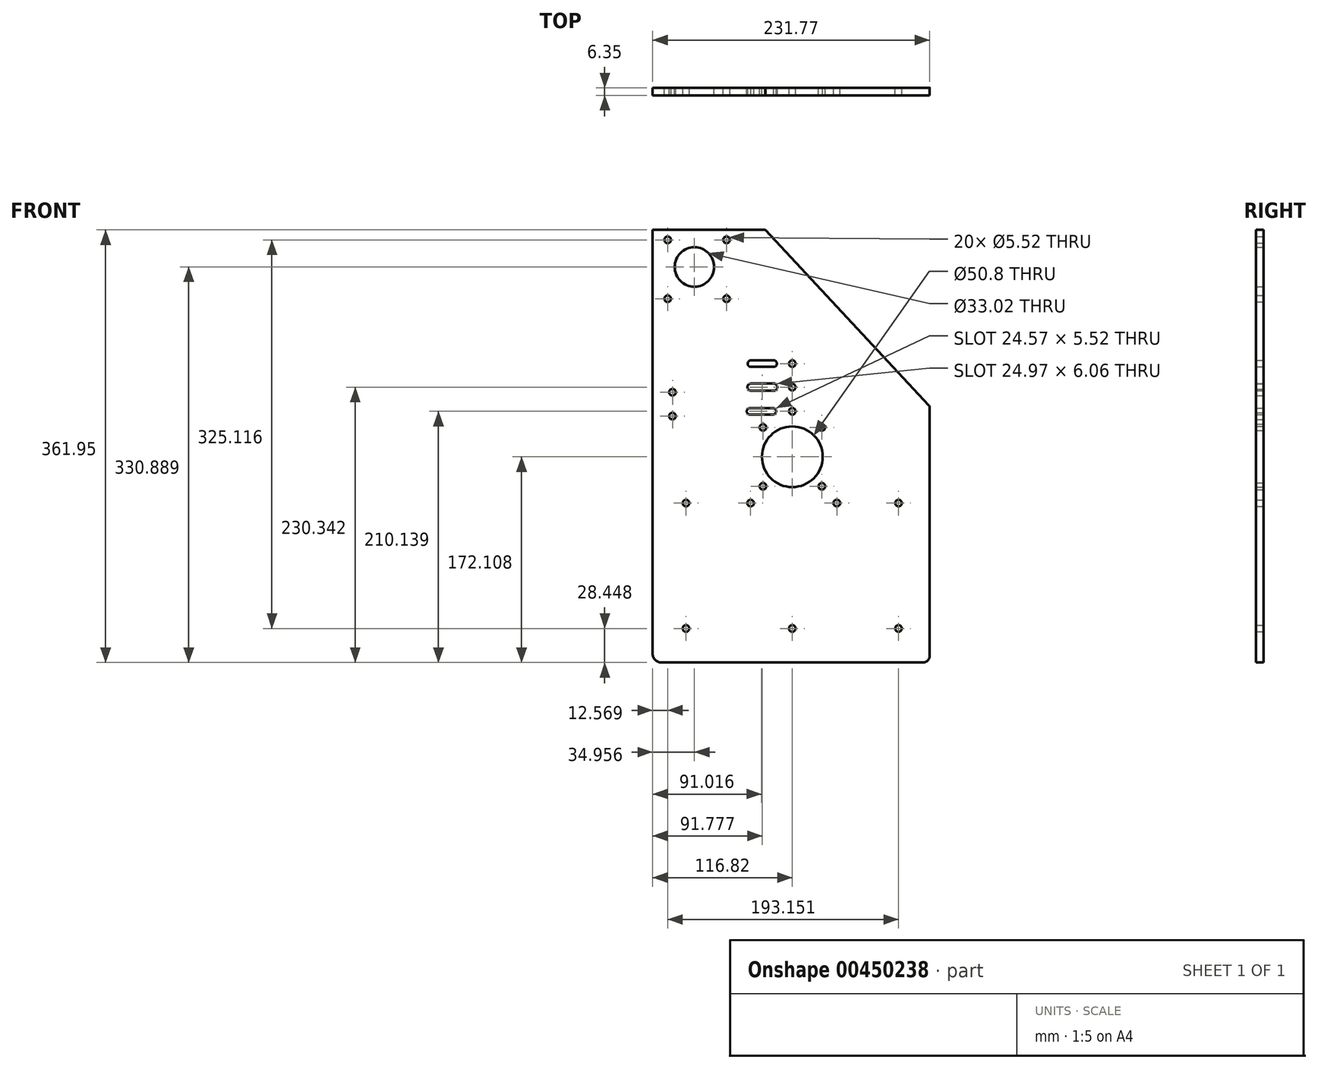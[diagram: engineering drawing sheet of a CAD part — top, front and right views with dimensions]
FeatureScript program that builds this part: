
annotation { "Feature Type Name" : "Feature", "Feature Type Description" : "" }
export const myFeature = defineFeature(function(context is Context, id is Id, definition is map)
    precondition{}
    {
        {
            var Q0;
            Q0=qCreatedBy(makeId("Front.planeOp"),FACE);
            var sketch = newSketch(context, id + "F0", { "sketchPlane" : qUnion([Q0])});
            skLineSegment(sketch, "E0.top", {"start": v(-109.54, -133.35) * mm, "end": v(109.54, -133.35) * mm});
            skLineSegment(sketch, "E0.left", {"start": v(-116.82, 228.6) * mm, "end": v(-116.82, -126.06) * mm});
            skPoint(sketch, "E0.middle", {"position": v(0, 0) * mm});
            skLineSegment(sketch, "E1", {"start": v(-22.65, 228.6) * mm, "end": v(114.3, 81.8) * mm});
            skLineSegment(sketch, "E2", {"start": v(114.95, 80.13) * mm, "end": v(114.95, -127.94) * mm});
            skCircle(sketch, "E3", {"center": v(-88.9, 0) * mm, "radius": 2.76 * mm});
            skCircle(sketch, "E4", {"center": v(-34.89, 0) * mm, "radius": 2.76 * mm});
            skCircle(sketch, "E5", {"center": v(37.25, 0) * mm, "radius": 2.76 * mm});
            skCircle(sketch, "E6", {"center": v(-88.9, -104.9) * mm, "radius": 2.76 * mm});
            skCircle(sketch, "E7", {"center": v(88.9, 0) * mm, "radius": 2.54 * mm});
            skCircle(sketch, "E8", {"center": v(88.9, 0) * mm, "radius": 2.76 * mm});
            skCircle(sketch, "E9", {"center": v(0, -104.9) * mm, "radius": 2.76 * mm});
            skPoint(sketch, "E10.visualSharp", {"position": v(114.95, 81.09) * mm});
            skArc(sketch, "E10.filletArc", {"start": v(114.95, 80.13) * mm, "mid": v(114.78, 81.02) * mm, "end": v(114.3, 81.8) * mm});
            skPoint(sketch, "E11.visualSharp", {"position": v(114.95, -133.35) * mm});
            skArc(sketch, "E11.filletArc", {"start": v(109.54, -133.35) * mm, "mid": v(113.37, -131.76) * mm, "end": v(114.95, -127.94) * mm});
            skPoint(sketch, "E12.visualSharp", {"position": v(-116.82, -133.35) * mm});
            skArc(sketch, "E12.filletArc", {"start": v(-116.82, -126.06) * mm, "mid": v(-114.7, -131.22) * mm, "end": v(-109.54, -133.35) * mm});
            skCircle(sketch, "E13", {"center": v(88.9, -104.9) * mm, "radius": 2.76 * mm});
            skCircle(sketch, "E14", {"center": v(0, 116.67) * mm, "radius": 2.76 * mm});
            skCircle(sketch, "E15", {"center": v(0, 97) * mm, "radius": 2.76 * mm});
            skCircle(sketch, "E16", {"center": v(0, 76.79) * mm, "radius": 2.76 * mm});
            skCircle(sketch, "E17", {"center": v(-100.24, 92.7) * mm, "radius": 2.76 * mm});
            skCircle(sketch, "E18", {"center": v(-100.24, 72.77) * mm, "radius": 2.76 * mm});
            skCircle(sketch, "E19", {"center": v(-104.25, 170.95) * mm, "radius": 2.76 * mm});
            skCircle(sketch, "E20", {"center": v(-104.25, 220.21) * mm, "radius": 2.76 * mm});
            skCircle(sketch, "E21", {"center": v(-24.52, 63.31) * mm, "radius": 2.76 * mm});
            skCircle(sketch, "E22", {"center": v(24.74, 63.31) * mm, "radius": 2.76 * mm});
            skCircle(sketch, "E23", {"center": v(-24.52, 14.04) * mm, "radius": 2.76 * mm});
            skCircle(sketch, "E24", {"center": v(24.74, 14.04) * mm, "radius": 2.76 * mm});
            skCircle(sketch, "E25", {"center": v(0, 38.76) * mm, "radius": 25.4 * mm});
            skLineSegment(sketch, "E26", {"start": v(-34.56, 119.43) * mm, "end": v(-15.62, 119.43) * mm});
            skLineSegment(sketch, "E27", {"start": v(-34.56, 113.9) * mm, "end": v(-15.62, 113.9) * mm});
            skLineSegment(sketch, "E28", {"start": v(-15.62, 93.96) * mm, "end": v(-34.56, 93.96) * mm});
            skLineSegment(sketch, "E29", {"start": v(-35.33, 79.55) * mm, "end": v(-16.28, 79.55) * mm});
            skLineSegment(sketch, "E30", {"start": v(-35.33, 74.03) * mm, "end": v(-16.28, 74.03) * mm});
            skArc(sketch, "E31", {"start": v(-15.62, 113.9) * mm, "mid": v(-12.86, 116.67) * mm, "end": v(-15.62, 119.43) * mm});
            skArc(sketch, "E32", {"start": v(-34.56, 119.43) * mm, "mid": v(-37.32, 116.67) * mm, "end": v(-34.56, 113.9) * mm});
            skArc(sketch, "E33", {"start": v(-16.28, 74.03) * mm, "mid": v(-13.52, 76.79) * mm, "end": v(-16.28, 79.55) * mm});
            skArc(sketch, "E34", {"start": v(-35.33, 79.55) * mm, "mid": v(-38.1, 76.79) * mm, "end": v(-35.33, 74.03) * mm});
            skLineSegment(sketch, "E35", {"start": v(-34.5, 100.02) * mm, "end": v(-15.6, 100.02) * mm});
            skArc(sketch, "E36", {"start": v(-15.62, 93.96) * mm, "mid": v(-12.56, 96.98) * mm, "end": v(-15.6, 100.02) * mm});
            skArc(sketch, "E37", {"start": v(-34.5, 100.02) * mm, "mid": v(-37.53, 97.02) * mm, "end": v(-34.56, 93.96) * mm});
            skCircle(sketch, "E38", {"center": v(-54.99, 170.95) * mm, "radius": 2.76 * mm});
            skCircle(sketch, "E39", {"center": v(-54.99, 220.21) * mm, "radius": 2.76 * mm});
            skLineSegment(sketch, "E40", {"start": v(-116.82, 228.6) * mm, "end": v(-22.65, 228.6) * mm});
            skCircle(sketch, "E41", {"center": v(-81.86, 197.54) * mm, "radius": 16.51 * mm});
            skSolve(sketch);
        }
        {
            var Q0;
            Q0=makeQuery(id+"F0.imprint","IMPRINT",FACE,{"disambiguationData":[TD([[makeQuery(id+"F0.imprint","IMPRINT",EDGE,{"derivedFrom":sQuery(id+"F0.wireOp",EDGE,"E0.top")}),1.0]])]});
            extrude(context, id + "F1", {"entities" : qUnion([Q0]), "depth" : 6.35 * mm, "offsetDistance" : 25.4 * mm});
        }
    });
